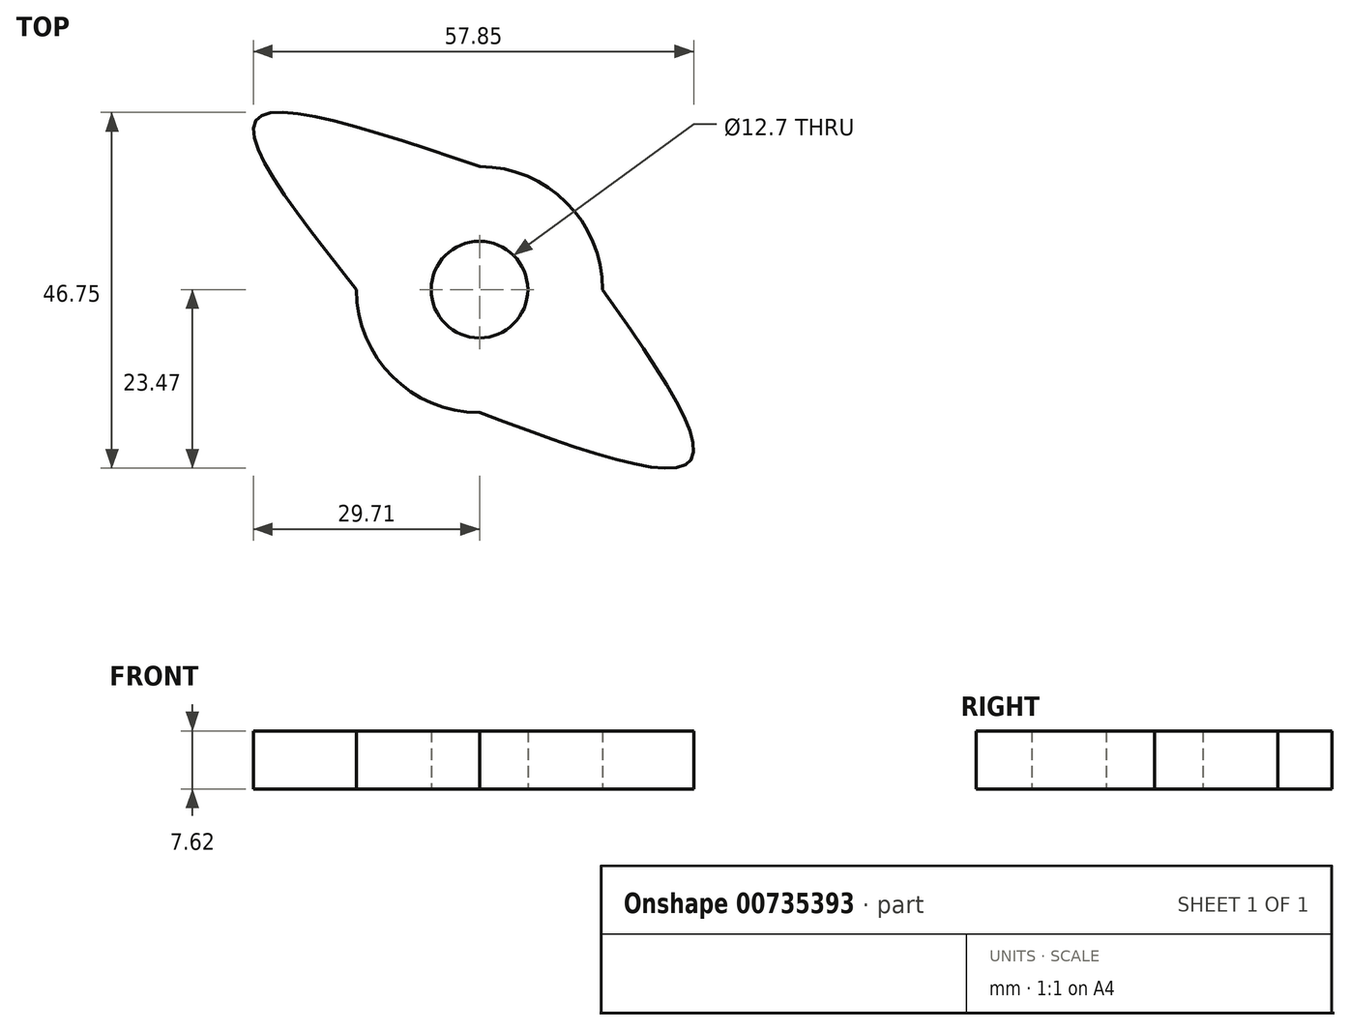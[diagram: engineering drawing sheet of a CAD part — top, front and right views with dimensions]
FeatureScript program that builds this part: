
annotation { "Feature Type Name" : "Feature", "Feature Type Description" : "" }
export const myFeature = defineFeature(function(context is Context, id is Id, definition is map)
    precondition{}
    {
        {
            var Q0;
            Q0=qCreatedBy(makeId("Top.planeOp"),FACE);
            var sketch = newSketch(context, id + "F0", { "sketchPlane" : qUnion([Q0])});
            skCircle(sketch, "E0", {"center": v(0, 0) * mm, "radius": 16.16 * mm});
            skFitSpline(sketch, "E1", {"points": [v(-16.16, 0) * mm, v(-29.36, 22.24) * mm, v(0, 16.16) * mm], "startDerivative": vector(-47.64, 60.14) * mm, "endDerivative": vector(78.42, -26.74) * mm});
            skFitSpline(sketch, "E2", {"points": [v(0, -16.16) * mm, v(27.7, -22.5) * mm, v(16.16, 0) * mm], "startDerivative": vector(73.82, -27.39) * mm, "endDerivative": vector(-42.63, 60.57) * mm});
            skEllipse(sketch, "E3", {"center": v(0, 0) * mm, "majorRadius": 6.35 * mm, "minorRadius": 6.35 * mm, "majorAxis": v(-0.52, -0.85)});
            skSolve(sketch);
        }
        {
            var Q0;
            Q0 = qSketchRegion(id + "F0", true);
            extrude(context, id + "F1", {"entities" : qUnion([Q0]), "depth" : 7.62 * mm, "offsetDistance" : 25.4 * mm});
        }
    });
